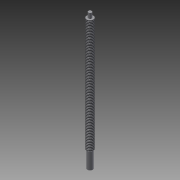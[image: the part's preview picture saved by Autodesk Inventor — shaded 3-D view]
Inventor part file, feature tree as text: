
AUTODESK INVENTOR PART (.ipt)
format: ipt  version: 2013 (Build 170138000, 138)  size: 83,456 bytes
history: native  units: in
note: dims shown in document units (in); Inventor stores cm internally (conversion verified against a paired STEP export)
features: extrude x3, sketch x3, thread x1
ambient origin geometry x8: Origin, YZ Plane, XZ Plane, XY Plane, X Axis, Y Axis, Z Axis, Center Point
bodies: Solid1 (feature_tree)
feature tree (7):
  extrude  "Extrusion1"  Depth=10.0in TaperAngle=0.0deg
  thread  "Thread1"  [1 undecoded]
  extrude  "Extrusion2"  Depth=0.105in
  extrude  "Extrusion3"  Depth=0.3937in
  sketch  "Sketch1"  dims[d0=0.5in d1=10.0in d2=0.0in d3=1.0in d4=0.0in]
  sketch  "Sketch2"  dims[d5=0.25in d6=0.105in]
  sketch  "Sketch3"  dims[d7=0.375in d8=0.0in d9=0.3937in d10=1.25in d11=0.0in]
note: 1 required parameter value undecoded (feature->parameter linkage not recoverable at this tier; creation-order binding heuristic only, values carry confidence <= 0.55)
